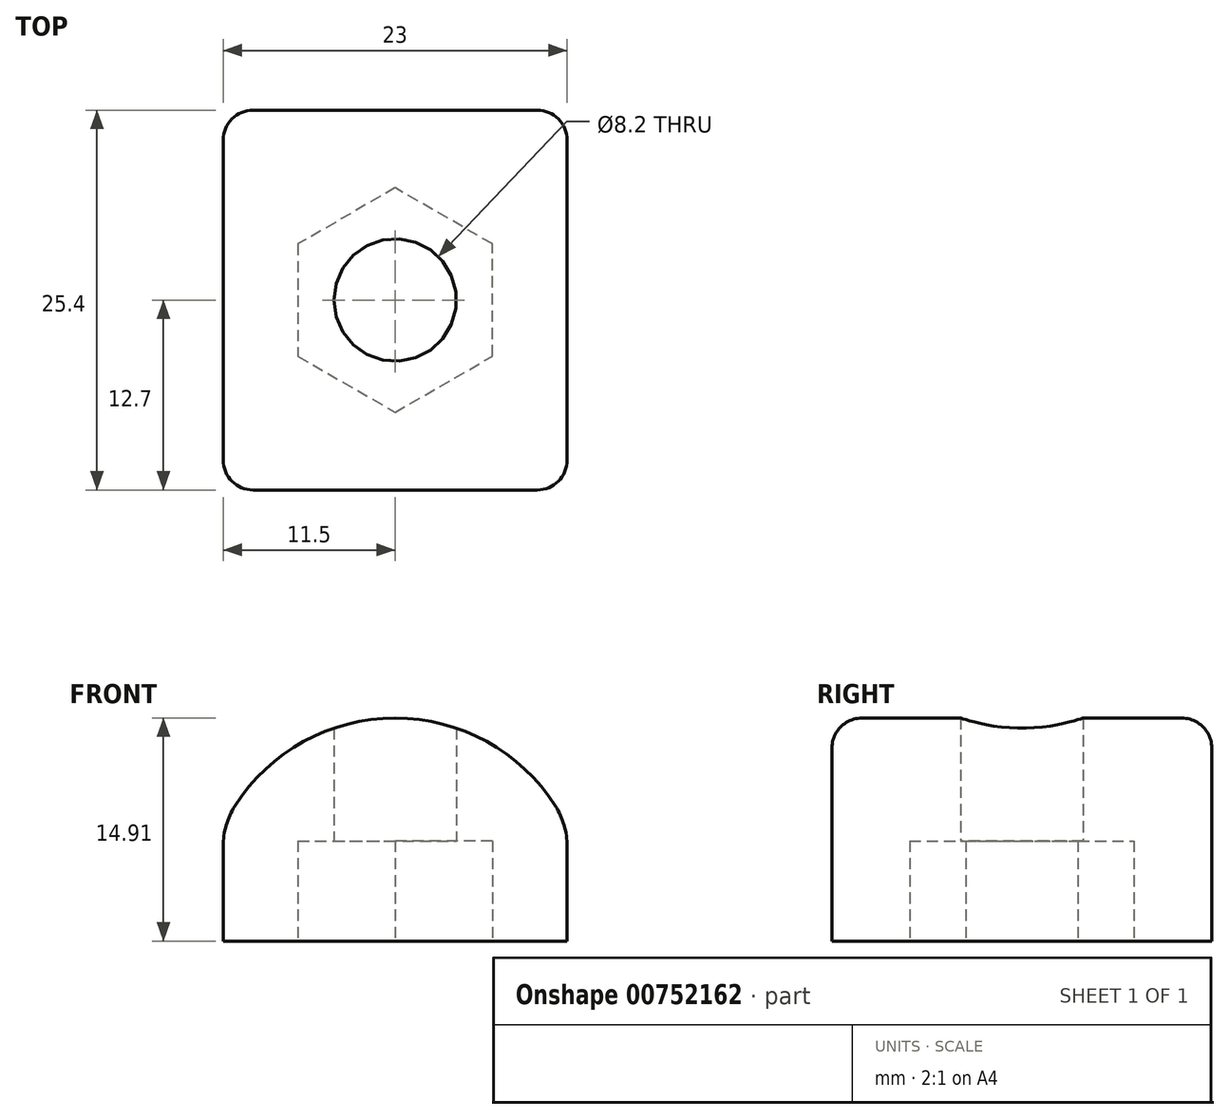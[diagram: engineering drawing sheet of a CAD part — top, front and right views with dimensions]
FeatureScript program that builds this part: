
annotation { "Feature Type Name" : "Feature", "Feature Type Description" : "" }
export const myFeature = defineFeature(function(context is Context, id is Id, definition is map)
    precondition{}
    {
        {
            var Q0;
            Q0=qCreatedBy(makeId("Front.planeOp"),FACE);
            var sketch = newSketch(context, id + "F0", { "sketchPlane" : qUnion([Q0])});
            skLineSegment(sketch, "E0.top", {"start": v(-11.5, -15) * mm, "end": v(11.5, -15) * mm});
            skLineSegment(sketch, "E0.left", {"start": v(-11.5, -7.4) * mm, "end": v(-11.5, -15) * mm});
            skLineSegment(sketch, "E0.right", {"start": v(11.5, -7.4) * mm, "end": v(11.5, -15) * mm});
            skArc(sketch, "E1", {"start": v(11.5, -7.4) * mm, "mid": v(0, -0.09) * mm, "end": v(-11.5, -7.4) * mm});
            skSolve(sketch);
        }
        {
            var Q0;
            Q0=makeQuery(id+"F0.imprint","IMPRINT",FACE,{"disambiguationData":[TD([[makeQuery(id+"F0.imprint","IMPRINT",EDGE,{"derivedFrom":sQuery(id+"F0.wireOp",EDGE,"E0.top")}),1.0]])]});
            extrude(context, id + "F1", {"entities" : qUnion([Q0]), "depth" : 25.4 * mm, "offsetDistance" : 25 * mm});
        }
        {
            var Q0;
            Q0=makeQuery(id+"F1.opExtrude","SWEPT_FACE",FACE,{"disambiguationData":[OSD([sQuery(id+"F0.wireOp",EDGE,"E0.top")])]});
            var sketch = newSketch(context, id + "F2", { "sketchPlane" : qUnion([Q0])});
            skCircle(sketch, "E2", {"center": v(0, 12.7) * mm, "radius": 4.1 * mm});
            skSolve(sketch);
        }
        {
            var Q0;
            Q0 = qSketchRegion(id + "F2", true);
            extrude(context, id + "F3", {"entities" : qUnion([Q0]), "operationType" : NewBodyOperationType.REMOVE, "oppositeDirection" : true, "depth" : 25 * mm, "offsetDistance" : 25 * mm});
        }
        {
            var Q0;
            Q0=makeQuery(id+"F1.opExtrude","SWEPT_FACE",FACE,{"disambiguationData":[OSD([sQuery(id+"F0.wireOp",EDGE,"E0.top")])]});
            var sketch = newSketch(context, id + "F4", { "sketchPlane" : qUnion([Q0])});
            skCircle(sketch, "E3.cCircle", {"center": v(0, 12.7) * mm, "radius": 6.5 * mm, "construction": true});
            skLineSegment(sketch, "E3.0", {"start": v(6.5, 8.95) * mm, "end": v(0, 5.2) * mm});
            skLineSegment(sketch, "E3.1", {"start": v(0, 5.2) * mm, "end": v(-6.5, 8.95) * mm});
            skLineSegment(sketch, "E3.2", {"start": v(-6.5, 8.95) * mm, "end": v(-6.5, 16.45) * mm});
            skLineSegment(sketch, "E3.3", {"start": v(-6.5, 16.45) * mm, "end": v(0, 20.2) * mm});
            skLineSegment(sketch, "E3.4", {"start": v(0, 20.2) * mm, "end": v(6.5, 16.45) * mm});
            skLineSegment(sketch, "E3.5", {"start": v(6.5, 16.45) * mm, "end": v(6.5, 8.95) * mm});
            skPoint(sketch, "E3.0.midPoint", {"position": v(3.25, 7.07) * mm});
            skSolve(sketch);
        }
        {
            var Q0;
            Q0 = qSketchRegion(id + "F4", true);
            extrude(context, id + "F5", {"entities" : qUnion([Q0]), "operationType" : NewBodyOperationType.REMOVE, "oppositeDirection" : true, "depth" : 6.7 * mm, "offsetDistance" : 25 * mm});
        }
        {
            var Q0;
            Q0=makeQuery(id+"F1.opExtrude","CAP_EDGE",EDGE,{"disambiguationData":[OSD([sQuery(id+"F0.wireOp",EDGE,"E1")])],"isStart":false});
            var Q1;
            Q1=makeQuery(id+"F1.opExtrude","CAP_EDGE",EDGE,{"disambiguationData":[OSD([sQuery(id+"F0.wireOp",EDGE,"E0.right")])],"isStart":false});
            var Q2;
            Q2=makeQuery(id+"F1.opExtrude","CAP_EDGE",EDGE,{"disambiguationData":[OSD([sQuery(id+"F0.wireOp",EDGE,"E0.left")])],"isStart":false});
            var Q3;
            Q3=makeQuery(id+"F1.opExtrude","CAP_EDGE",EDGE,{"disambiguationData":[OSD([sQuery(id+"F0.wireOp",EDGE,"E0.right")])],"isStart":true});
            var Q4;
            Q4=makeQuery(id+"F1.opExtrude","CAP_EDGE",EDGE,{"disambiguationData":[OSD([sQuery(id+"F0.wireOp",EDGE,"E1")])],"isStart":true});
            var Q5;
            Q5=makeQuery(id+"F1.opExtrude","CAP_EDGE",EDGE,{"disambiguationData":[OSD([sQuery(id+"F0.wireOp",EDGE,"E0.left")])],"isStart":true});
            fillet(context, id + "F6", {"entities" : qUnion([Q0, Q1, Q2, Q3, Q4, Q5]), "radius" : 2 * mm, "tangentPropagation" : true, "allowEdgeOverflow" : false});
        }
        {
            var Q0;
            Q0=makeQuery(id+"F1.opExtrude","SWEPT_EDGE",EDGE,{"disambiguationData":[OSD([sQuery(id+"F0.wireOp",EDGE,"E0.right"),sQuery(id+"F0.wireOp",EDGE,"E1")])]});
            var Q1;
            Q1=makeQuery(id+"F1.opExtrude","SWEPT_EDGE",EDGE,{"disambiguationData":[OSD([sQuery(id+"F0.wireOp",EDGE,"E0.left"),sQuery(id+"F0.wireOp",EDGE,"E1")])]});
            fillet(context, id + "F7", {"entities" : qUnion([Q0, Q1]), "radius" : 5 * mm, "tangentPropagation" : true, "allowEdgeOverflow" : false});
        }
    });
